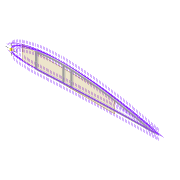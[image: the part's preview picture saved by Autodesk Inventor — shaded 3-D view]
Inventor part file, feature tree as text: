
AUTODESK INVENTOR PART (.ipt)
format: ipt  version: 2022 (Build 260153000, 153)  size: 369,664 bytes
history: native  units: mm
features: extrude x7, sketch x7, projected_geometry x5, shell x1, fillet x1, plane x1
ambient origin geometry x8: Origin, YZ Plane, XZ Plane, XY Plane, X Axis, Y Axis, Z Axis, Center Point
bodies: Solid1 (feature_tree)
feature tree (22):
  extrude  "Extrusion1"  Depth=5.0mm
  shell  "Shell1"  Thickness=2.0mm
  extrude  "Extrusion8"  Depth=5.9mm
  extrude  "Extrusion3"  Depth=10.0mm TaperAngle=0.0deg
  extrude  "Extrusion4"  Depth=2.0mm
  fillet  "Fillet1"  Radius=5.0mm
  extrude  "Extrusion5"  Depth=2.5mm
  plane  "Work Plane2"
  extrude  "Extrusion9"  Depth=1.6mm
  extrude  "Extrusion10"  Depth=0.5mm
  sketch  "Sketch3"  dims[d0=4.0mm d1=0.0mm d2=5.0mm d7=2.0mm]
  sketch  "Sketch8"  dims[d8=2.0mm d9=5.9mm]
  sketch  "Sketch9"  dims[d13=10.0mm d14=0.0mm d16=10.0mm d17=0.0mm]
  sketch  "Sketch10"  dims[d22=4.0mm d23=0.0mm d31=2.0mm d32=5.0mm]
  projected_geometry  "Projected Loop4"
  projected_geometry  "Projected Loop10"
  sketch  "Sketch24"  dims[d34=1.6mm d35=2.5mm]
  projected_geometry  "Projected Loop11"
  projected_geometry  "Projected Loop12"
  sketch  "Sketch26"  dims[d37=5.0mm d38=1.6mm]
  projected_geometry  "Projected Loop13"
  sketch  "Sketch27"  dims[d40=2.5mm d62=77.0mm d63=6.0mm d64=4.0mm d65=0.0mm d66=3.0mm d67=12.0mm d68=80.0mm d69=20.0mm d70=0.5mm d71=10.0mm d72=0.0mm d73=10.0mm d74=0.0mm]
